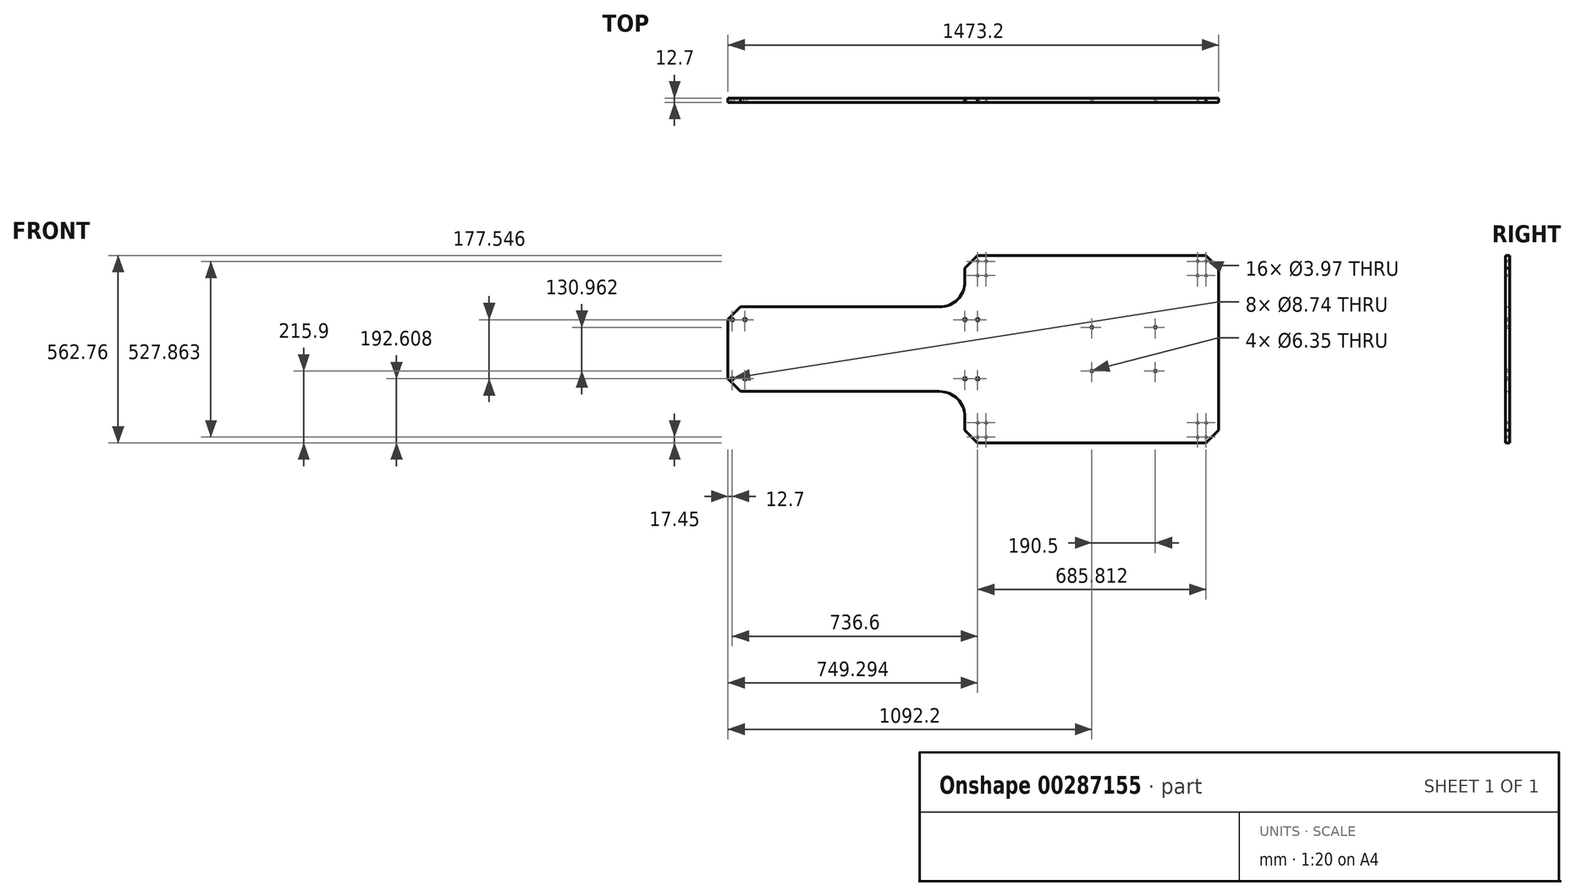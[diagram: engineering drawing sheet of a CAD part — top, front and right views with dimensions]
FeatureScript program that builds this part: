
annotation { "Feature Type Name" : "Feature", "Feature Type Description" : "" }
export const myFeature = defineFeature(function(context is Context, id is Id, definition is map)
    precondition{}
    {
        {
            var Q0;
            Q0=qCreatedBy(makeId("Front.planeOp"),FACE);
            var sketch = newSketch(context, id + "F0", { "sketchPlane" : qUnion([Q0])});
            skLineSegment(sketch, "E0", {"start": v(711.2, 0) * mm, "end": v(1473.2, 0) * mm});
            skLineSegment(sketch, "E1.0", {"start": v(711.2, 562.76) * mm, "end": v(1473.2, 562.76) * mm});
            skLineSegment(sketch, "E2", {"start": v(1473.2, 562.76) * mm, "end": v(1473.2, 0) * mm});
            skLineSegment(sketch, "E3.0", {"start": v(711.2, 0) * mm, "end": v(711.2, 78.18) * mm});
            skLineSegment(sketch, "E4.0", {"start": v(635, 408.38) * mm, "end": v(0, 408.38) * mm});
            skLineSegment(sketch, "E5.MirrorCS", {"start": v(635, 154.38) * mm, "end": v(0, 154.38) * mm});
            skLineSegment(sketch, "E6.trimOffspring", {"start": v(711.2, 484.58) * mm, "end": v(711.2, 562.76) * mm});
            skArc(sketch, "E7.filletArc", {"start": v(635, 408.38) * mm, "mid": v(688.88, 430.7) * mm, "end": v(711.2, 484.58) * mm});
            skArc(sketch, "E8.filletArc", {"start": v(711.2, 78.18) * mm, "mid": v(688.88, 132.06) * mm, "end": v(635, 154.38) * mm});
            skLineSegment(sketch, "E9", {"start": v(0, 408.38) * mm, "end": v(0, 154.38) * mm});
            skSolve(sketch);
        }
        {
            var Q0;
            Q0=qSketchRegion(id+"F0",true);
            extrude(context, id + "F1", {"entities" : qUnion([Q0]), "depth" : 12.7 * mm});
        }
        {
            var Q0;
            Q0=makeQuery(id+"F1.opExtrude","SWEPT_EDGE",EDGE,{"disambiguationData":[OSD([sQuery(id+"F0.wireOp",EDGE,"E1.0"),sQuery(id+"F0.wireOp",EDGE,"E6.trimOffspring")])]});
            var Q1;
            Q1=makeQuery(id+"F1.opExtrude","SWEPT_EDGE",EDGE,{"disambiguationData":[OSD([sQuery(id+"F0.wireOp",EDGE,"E0"),sQuery(id+"F0.wireOp",EDGE,"E3.0")])]});
            var Q2;
            Q2=makeQuery(id+"F1.opExtrude","SWEPT_EDGE",EDGE,{"disambiguationData":[OSD([sQuery(id+"F0.wireOp",EDGE,"E0"),sQuery(id+"F0.wireOp",EDGE,"E2")])]});
            var Q3;
            Q3=makeQuery(id+"F1.opExtrude","SWEPT_EDGE",EDGE,{"disambiguationData":[OSD([sQuery(id+"F0.wireOp",EDGE,"E1.0"),sQuery(id+"F0.wireOp",EDGE,"E2")])]});
            var Q4;
            Q4=makeQuery(id+"F1.opExtrude","SWEPT_EDGE",EDGE,{"disambiguationData":[OSD([sQuery(id+"F0.wireOp",EDGE,"E5.MirrorCS"),sQuery(id+"F0.wireOp",EDGE,"E9")])]});
            var Q5;
            Q5=makeQuery(id+"F1.opExtrude","SWEPT_EDGE",EDGE,{"disambiguationData":[OSD([sQuery(id+"F0.wireOp",EDGE,"E4.0"),sQuery(id+"F0.wireOp",EDGE,"E9")])]});
            chamfer(context, id + "F2", {"entities" : qUnion([Q0, Q1, Q2, Q3, Q4, Q5]), "chamferType" : ChamferType.OFFSET_ANGLE, "width" : 38.1 * mm, "oppositeDirection" : false, "angle" : 45 * degree, "tangentPropagation" : true});
        }
        {
            var Q0;
            Q0=makeQuery(id+"F1.opExtrude","CAP_FACE",FACE,{"disambiguationData":[OSD([sQuery(id+"F0.wireOp",EDGE,"E0"),sQuery(id+"F0.wireOp",EDGE,"E1.0"),sQuery(id+"F0.wireOp",EDGE,"E2"),sQuery(id+"F0.wireOp",EDGE,"E3.0"),sQuery(id+"F0.wireOp",EDGE,"E4.0"),sQuery(id+"F0.wireOp",EDGE,"E5.MirrorCS"),sQuery(id+"F0.wireOp",EDGE,"E6.trimOffspring"),sQuery(id+"F0.wireOp",EDGE,"E7.filletArc"),sQuery(id+"F0.wireOp",EDGE,"E8.filletArc"),sQuery(id+"F0.wireOp",EDGE,"E9")])],"isStart":false});
            var sketch = newSketch(context, id + "F3", { "sketchPlane" : qUnion([Q0])});
            skCircle(sketch, "E10", {"center": v(1282.7, 346.86) * mm, "radius": 3.18 * mm});
            skCircle(sketch, "E11", {"center": v(1282.7, 215.9) * mm, "radius": 3.18 * mm});
            skPoint(sketch, "E12.endSnap0", {"position": v(1092.2, 215.9) * mm});
            skCircle(sketch, "E13", {"center": v(1092.2, 346.86) * mm, "radius": 3.18 * mm});
            skCircle(sketch, "E14", {"center": v(1092.2, 215.9) * mm, "radius": 3.18 * mm});
            skLineSegment(sketch, "E15", {"start": v(1282.7, 346.86) * mm, "end": v(500.57, 346.86) * mm});
            skLineSegment(sketch, "E16", {"start": v(1282.7, 215.9) * mm, "end": v(476.65, 215.9) * mm});
            skSolve(sketch);
        }
        {
            var Q0;
            Q0=sQuery(id+"F3.wireOp",VERTEX,"E12.endSnap0");
            var Q1;
            Q1=sQuery(id+"F3.wireOp",VERTEX,"E13.center");
            var Q2;
            Q2=sQuery(id+"F3.wireOp",VERTEX,"E10.center");
            var Q3;
            Q3=sQuery(id+"F3.wireOp",VERTEX,"E11.center");
            var Q4;
            Q4=makeQuery(id+"F1.opExtrude","SWEPT_BODY",BODY,{"disambiguationData":[OSD([sQuery(id+"F0.wireOp",EDGE,"E0"),sQuery(id+"F0.wireOp",EDGE,"E1.0"),sQuery(id+"F0.wireOp",EDGE,"E2"),sQuery(id+"F0.wireOp",EDGE,"E3.0"),sQuery(id+"F0.wireOp",EDGE,"E4.0"),sQuery(id+"F0.wireOp",EDGE,"E5.MirrorCS"),sQuery(id+"F0.wireOp",EDGE,"E6.trimOffspring"),sQuery(id+"F0.wireOp",EDGE,"E7.filletArc"),sQuery(id+"F0.wireOp",EDGE,"E8.filletArc"),sQuery(id+"F0.wireOp",EDGE,"E9")])]});
            hole(context, id + "F4", {"style" : HoleStyle.SIMPLE, "endStyle" : HoleEndStyle.THROUGH, "holeDiameter" : 6.35 * mm, "tappedDepth" : 12.7 * mm, "tapClearance" : 3, "locations" : qUnion([Q0, Q1, Q2, Q3]), "scope" : qUnion([Q4])});
        }
        {
            var Q0;
            Q0=makeQuery(id+"F1.opExtrude","CAP_FACE",FACE,{"disambiguationData":[OSD([sQuery(id+"F0.wireOp",EDGE,"E0"),sQuery(id+"F0.wireOp",EDGE,"E1.0"),sQuery(id+"F0.wireOp",EDGE,"E2"),sQuery(id+"F0.wireOp",EDGE,"E3.0"),sQuery(id+"F0.wireOp",EDGE,"E4.0"),sQuery(id+"F0.wireOp",EDGE,"E5.MirrorCS"),sQuery(id+"F0.wireOp",EDGE,"E6.trimOffspring"),sQuery(id+"F0.wireOp",EDGE,"E7.filletArc"),sQuery(id+"F0.wireOp",EDGE,"E8.filletArc"),sQuery(id+"F0.wireOp",EDGE,"E9")])],"isStart":false});
            var sketch = newSketch(context, id + "F5", { "sketchPlane" : qUnion([Q0])});
            skLineSegment(sketch, "E17", {"start": v(1422.4, 38.89) * mm, "end": v(1422.4, 0) * mm});
            skPoint(sketch, "E18", {"position": v(1422.4, 38.89) * mm});
            skLineSegment(sketch, "E19", {"start": v(1422.4, 38.89) * mm, "end": v(1422.4, 60.32) * mm});
            skLineSegment(sketch, "E20", {"start": v(1422.4, 60.32) * mm, "end": v(1435.1, 60.32) * mm});
            skLineSegment(sketch, "E21.MirrorCS", {"start": v(1422.4, 60.32) * mm, "end": v(1409.7, 60.32) * mm});
            skPoint(sketch, "E22", {"position": v(1409.7, 60.32) * mm});
            skPoint(sketch, "E23", {"position": v(1435.1, 60.32) * mm});
            skLineSegment(sketch, "E24", {"start": v(1422.4, 38.89) * mm, "end": v(1395.35, 38.89) * mm});
            skLineSegment(sketch, "E25.MirrorCS", {"start": v(1422.4, 17.45) * mm, "end": v(1409.7, 17.45) * mm});
            skLineSegment(sketch, "E26.MirrorCS", {"start": v(1422.4, 17.45) * mm, "end": v(1435.1, 17.45) * mm});
            skPoint(sketch, "E27", {"position": v(1409.7, 17.45) * mm});
            skPoint(sketch, "E28", {"position": v(1435.1, 17.45) * mm});
            skLineSegment(sketch, "E29.MirrorCS", {"start": v(762, 60.32) * mm, "end": v(774.7, 60.32) * mm});
            skLineSegment(sketch, "E30.MirrorCS", {"start": v(762, 38.89) * mm, "end": v(762, 60.32) * mm});
            skLineSegment(sketch, "E31.MirrorCS", {"start": v(762, 17.45) * mm, "end": v(774.7, 17.45) * mm});
            skLineSegment(sketch, "E32.MirrorCS", {"start": v(762, 60.32) * mm, "end": v(749.3, 60.32) * mm});
            skLineSegment(sketch, "E33.MirrorCS", {"start": v(762, 17.45) * mm, "end": v(749.3, 17.45) * mm});
            skLineSegment(sketch, "E34.MirrorCS", {"start": v(762, 38.89) * mm, "end": v(789.05, 38.89) * mm});
            skLineSegment(sketch, "E35.MirrorCS", {"start": v(762, 38.89) * mm, "end": v(762, 0) * mm});
            skPoint(sketch, "E36.MirrorP", {"position": v(762, 38.89) * mm});
            skPoint(sketch, "E37.MirrorP", {"position": v(749.3, 60.32) * mm});
            skPoint(sketch, "E38.MirrorP", {"position": v(749.3, 17.45) * mm});
            skPoint(sketch, "E39.MirrorP", {"position": v(774.7, 17.45) * mm});
            skPoint(sketch, "E40.MirrorP", {"position": v(774.7, 60.32) * mm});
            skLineSegment(sketch, "E41.MirrorCS", {"start": v(1422.4, 523.88) * mm, "end": v(1422.4, 502.44) * mm});
            skLineSegment(sketch, "E42.MirrorCS", {"start": v(1422.4, 502.44) * mm, "end": v(1409.7, 502.44) * mm});
            skLineSegment(sketch, "E43.MirrorCS", {"start": v(1422.4, 545.31) * mm, "end": v(1409.7, 545.31) * mm});
            skLineSegment(sketch, "E44.MirrorCS", {"start": v(1422.4, 502.44) * mm, "end": v(1435.1, 502.44) * mm});
            skLineSegment(sketch, "E45.MirrorCS", {"start": v(1422.4, 545.31) * mm, "end": v(1435.1, 545.31) * mm});
            skLineSegment(sketch, "E46.MirrorCS", {"start": v(1422.4, 523.88) * mm, "end": v(1422.4, 562.76) * mm});
            skLineSegment(sketch, "E47.MirrorCS", {"start": v(1422.4, 523.88) * mm, "end": v(1395.35, 523.88) * mm});
            skPoint(sketch, "E48.MirrorP", {"position": v(1422.4, 523.88) * mm});
            skPoint(sketch, "E49.MirrorP", {"position": v(1435.1, 502.44) * mm});
            skPoint(sketch, "E50.MirrorP", {"position": v(1409.7, 545.31) * mm});
            skPoint(sketch, "E51.MirrorP", {"position": v(1435.1, 545.31) * mm});
            skPoint(sketch, "E52.MirrorP", {"position": v(1409.7, 502.44) * mm});
            skLineSegment(sketch, "E53.MirrorCS", {"start": v(762, 545.31) * mm, "end": v(774.7, 545.31) * mm});
            skLineSegment(sketch, "E54.MirrorCS", {"start": v(762, 523.88) * mm, "end": v(762, 502.44) * mm});
            skLineSegment(sketch, "E55.MirrorCS", {"start": v(762, 502.44) * mm, "end": v(774.7, 502.44) * mm});
            skLineSegment(sketch, "E56.MirrorCS", {"start": v(762, 502.44) * mm, "end": v(749.3, 502.44) * mm});
            skLineSegment(sketch, "E57.MirrorCS", {"start": v(762, 545.31) * mm, "end": v(749.3, 545.31) * mm});
            skLineSegment(sketch, "E58.MirrorCS", {"start": v(762, 523.88) * mm, "end": v(789.05, 523.88) * mm});
            skLineSegment(sketch, "E59.MirrorCS", {"start": v(762, 523.88) * mm, "end": v(762, 562.76) * mm});
            skPoint(sketch, "E60.MirrorP", {"position": v(774.7, 545.31) * mm});
            skPoint(sketch, "E61.MirrorP", {"position": v(749.3, 545.31) * mm});
            skPoint(sketch, "E62.MirrorP", {"position": v(762, 523.88) * mm});
            skPoint(sketch, "E63.MirrorP", {"position": v(749.3, 502.44) * mm});
            skPoint(sketch, "E64.MirrorP", {"position": v(774.7, 502.44) * mm});
            skLineSegment(sketch, "E65", {"start": v(0, 281.38) * mm, "end": v(0, 192.6) * mm});
            skLineSegment(sketch, "E66.0", {"start": v(12.7, 281.38) * mm, "end": v(12.7, 192.6) * mm});
            skLineSegment(sketch, "E67.0", {"start": v(50.8, 281.38) * mm, "end": v(50.8, 192.6) * mm});
            skLineSegment(sketch, "E68", {"start": v(0, 281.38) * mm, "end": v(134.45, 281.38) * mm});
            skCircle(sketch, "E69", {"center": v(12.7, 192.6) * mm, "radius": 4.37 * mm});
            skCircle(sketch, "E70", {"center": v(50.8, 192.6) * mm, "radius": 4.37 * mm});
            skCircle(sketch, "E71.MirrorC", {"center": v(50.8, 370.15) * mm, "radius": 4.37 * mm});
            skCircle(sketch, "E72.MirrorC", {"center": v(12.7, 370.15) * mm, "radius": 4.37 * mm});
            skLineSegment(sketch, "E73", {"start": v(0, 281.38) * mm, "end": v(381, 281.38) * mm});
            skLineSegment(sketch, "E74", {"start": v(381, 281.38) * mm, "end": v(381, 256.55) * mm});
            skCircle(sketch, "E75.MirrorC", {"center": v(711.2, 370.15) * mm, "radius": 4.37 * mm});
            skCircle(sketch, "E76.MirrorC", {"center": v(749.3, 370.15) * mm, "radius": 4.37 * mm});
            skCircle(sketch, "E77.MirrorC", {"center": v(749.3, 192.6) * mm, "radius": 4.37 * mm});
            skCircle(sketch, "E78.MirrorC", {"center": v(711.2, 192.6) * mm, "radius": 4.37 * mm});
            skSolve(sketch);
        }
        {
            var Q0;
            Q0=sQuery(id+"F5.wireOp",VERTEX,"E61.MirrorP");
            var Q1;
            Q1=sQuery(id+"F5.wireOp",VERTEX,"E63.MirrorP");
            var Q2;
            Q2=sQuery(id+"F5.wireOp",VERTEX,"E64.MirrorP");
            var Q3;
            Q3=sQuery(id+"F5.wireOp",VERTEX,"E60.MirrorP");
            var Q4;
            Q4=sQuery(id+"F5.wireOp",VERTEX,"E37.MirrorP");
            var Q5;
            Q5=sQuery(id+"F5.wireOp",VERTEX,"E39.MirrorP");
            var Q6;
            Q6=sQuery(id+"F5.wireOp",VERTEX,"E38.MirrorP");
            var Q7;
            Q7=sQuery(id+"F5.wireOp",VERTEX,"E40.MirrorP");
            var Q8;
            Q8=sQuery(id+"F5.wireOp",VERTEX,"E52.MirrorP");
            var Q9;
            Q9=sQuery(id+"F5.wireOp",VERTEX,"E49.MirrorP");
            var Q10;
            Q10=sQuery(id+"F5.wireOp",VERTEX,"E51.MirrorP");
            var Q11;
            Q11=sQuery(id+"F5.wireOp",VERTEX,"E50.MirrorP");
            var Q12;
            Q12=sQuery(id+"F5.wireOp",VERTEX,"E27");
            var Q13;
            Q13=sQuery(id+"F5.wireOp",VERTEX,"E28");
            var Q14;
            Q14=sQuery(id+"F5.wireOp",VERTEX,"E23");
            var Q15;
            Q15=sQuery(id+"F5.wireOp",VERTEX,"E22");
            var Q16;
            Q16=makeQuery(id+"F1.opExtrude","SWEPT_BODY",BODY,{"disambiguationData":[OSD([sQuery(id+"F0.wireOp",EDGE,"E0"),sQuery(id+"F0.wireOp",EDGE,"E1.0"),sQuery(id+"F0.wireOp",EDGE,"E2"),sQuery(id+"F0.wireOp",EDGE,"E3.0"),sQuery(id+"F0.wireOp",EDGE,"E4.0"),sQuery(id+"F0.wireOp",EDGE,"E5.MirrorCS"),sQuery(id+"F0.wireOp",EDGE,"E6.trimOffspring"),sQuery(id+"F0.wireOp",EDGE,"E7.filletArc"),sQuery(id+"F0.wireOp",EDGE,"E8.filletArc"),sQuery(id+"F0.wireOp",EDGE,"E9")])]});
            hole(context, id + "F6", {"style" : HoleStyle.SIMPLE, "endStyle" : HoleEndStyle.THROUGH, "holeDiameter" : 3.97 * mm, "tappedDepth" : 12.7 * mm, "tapClearance" : 3, "locations" : qUnion([Q0, Q1, Q2, Q3, Q4, Q5, Q6, Q7, Q8, Q9, Q10, Q11, Q12, Q13, Q14, Q15]), "scope" : qUnion([Q16])});
        }
        {
            var Q0;
            Q0=sQuery(id+"F5.wireOp",VERTEX,"E72.MirrorC.center");
            var Q1;
            Q1=sQuery(id+"F5.wireOp",VERTEX,"E71.MirrorC.center");
            var Q2;
            Q2=sQuery(id+"F5.wireOp",VERTEX,"E69.center");
            var Q3;
            Q3=sQuery(id+"F5.wireOp",VERTEX,"E70.center");
            var Q4;
            Q4=sQuery(id+"F5.wireOp",VERTEX,"E75.MirrorC.center");
            var Q5;
            Q5=sQuery(id+"F5.wireOp",VERTEX,"E76.MirrorC.center");
            var Q6;
            Q6=sQuery(id+"F5.wireOp",VERTEX,"E78.MirrorC.center");
            var Q7;
            Q7=sQuery(id+"F5.wireOp",VERTEX,"E77.MirrorC.center");
            var Q8;
            Q8=makeQuery(id+"F1.opExtrude","SWEPT_BODY",BODY,{"disambiguationData":[OSD([sQuery(id+"F0.wireOp",EDGE,"E0"),sQuery(id+"F0.wireOp",EDGE,"E1.0"),sQuery(id+"F0.wireOp",EDGE,"E2"),sQuery(id+"F0.wireOp",EDGE,"E3.0"),sQuery(id+"F0.wireOp",EDGE,"E4.0"),sQuery(id+"F0.wireOp",EDGE,"E5.MirrorCS"),sQuery(id+"F0.wireOp",EDGE,"E6.trimOffspring"),sQuery(id+"F0.wireOp",EDGE,"E7.filletArc"),sQuery(id+"F0.wireOp",EDGE,"E8.filletArc"),sQuery(id+"F0.wireOp",EDGE,"E9")])]});
            hole(context, id + "F7", {"style" : HoleStyle.SIMPLE, "endStyle" : HoleEndStyle.THROUGH, "holeDiameter" : 8.74 * mm, "tappedDepth" : 12.7 * mm, "tapClearance" : 3, "locations" : qUnion([Q0, Q1, Q2, Q3, Q4, Q5, Q6, Q7]), "scope" : qUnion([Q8])});
        }
    });
